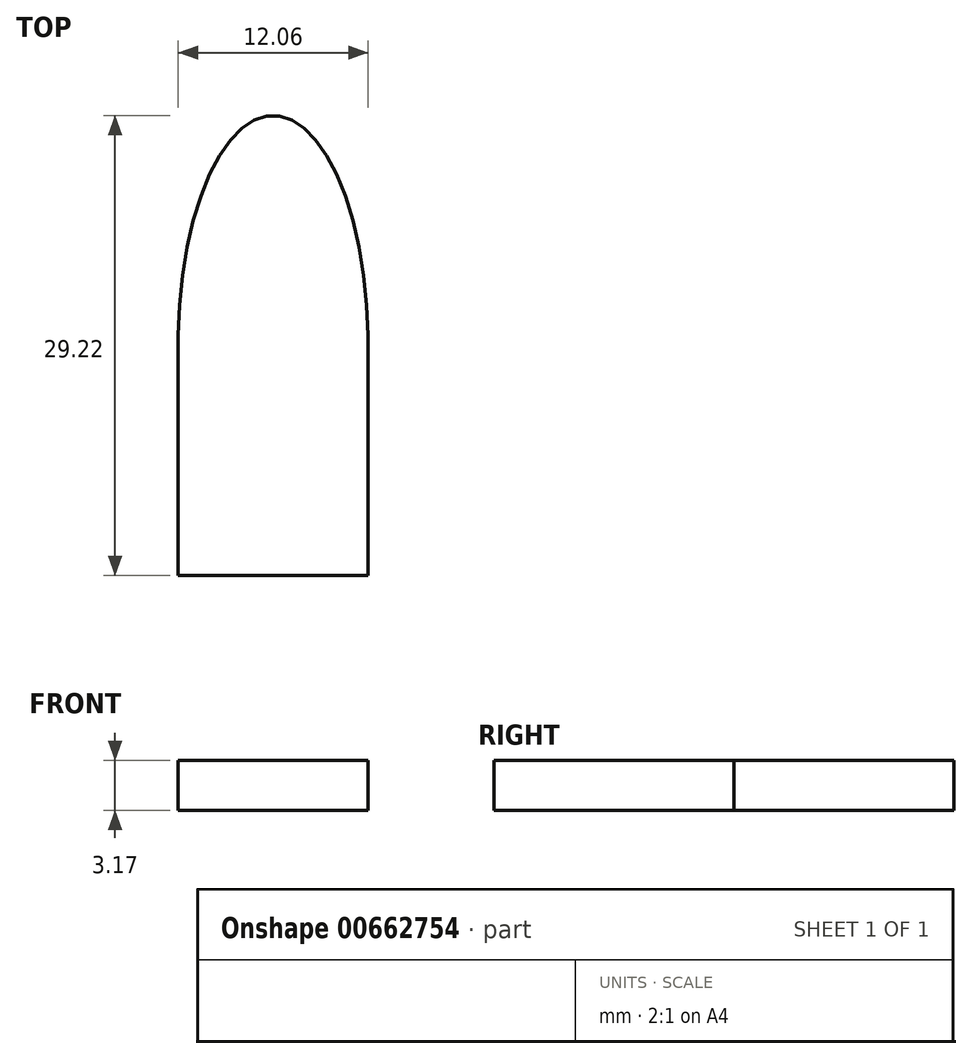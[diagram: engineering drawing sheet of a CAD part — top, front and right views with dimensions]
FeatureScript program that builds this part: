
annotation { "Feature Type Name" : "Feature", "Feature Type Description" : "" }
export const myFeature = defineFeature(function(context is Context, id is Id, definition is map)
    precondition{}
    {
        {
            var Q0;
            Q0=qCreatedBy(makeId("Top.planeOp"),FACE);
            var sketch = newSketch(context, id + "F0", { "sketchPlane" : qUnion([Q0])});
            skLineSegment(sketch, "E0.bottom", {"start": v(6.03, -14.6) * mm, "end": v(-6.03, -14.6) * mm});
            skLineSegment(sketch, "E0.left", {"start": v(6.03, -14.6) * mm, "end": v(6.03, 0.64) * mm});
            skLineSegment(sketch, "E0.right", {"start": v(-6.03, -14.6) * mm, "end": v(-6.03, 0.63) * mm});
            skPoint(sketch, "E0.middle", {"position": v(0, 0) * mm});
            skPoint(sketch, "E1", {"position": v(0, 14.6) * mm});
            skPoint(sketch, "E2", {"position": v(-6.03, 0.63) * mm});
            skEllipticalArc(sketch, "E3", {});
            skPoint(sketch, "E4.orphan", {"position": v(6.03, 14.6) * mm});
            skPoint(sketch, "E0.top.end.orphan", {"position": v(-6.03, 14.6) * mm});
            const initialGuessF0  = {"E3": [0, 0, 0, 1, 0.014605, 0.006038209892428299, 4.6688970095945646, 1.6142882975850208]};
            skSetInitialGuess(sketch, initialGuessF0);
            skSolve(sketch);
        }
        {
            var Q0;
            {var subQ1=sQuery(id+"F0.wireOp",EDGE,"E0.bottom");Q0=makeQuery(id+"F0.imprint","IMPRINT",FACE,{"disambiguationData":[TD([[makeQuery(id+"F0.imprint","IMPRINT",EDGE,{"derivedFrom":subQ1}),-1.0]])]});}
            extrude(context, id + "F1", {"entities" : qUnion([Q0]), "depth" : 3.17 * mm, "offsetDistance" : 25.4 * mm});
        }
    });
